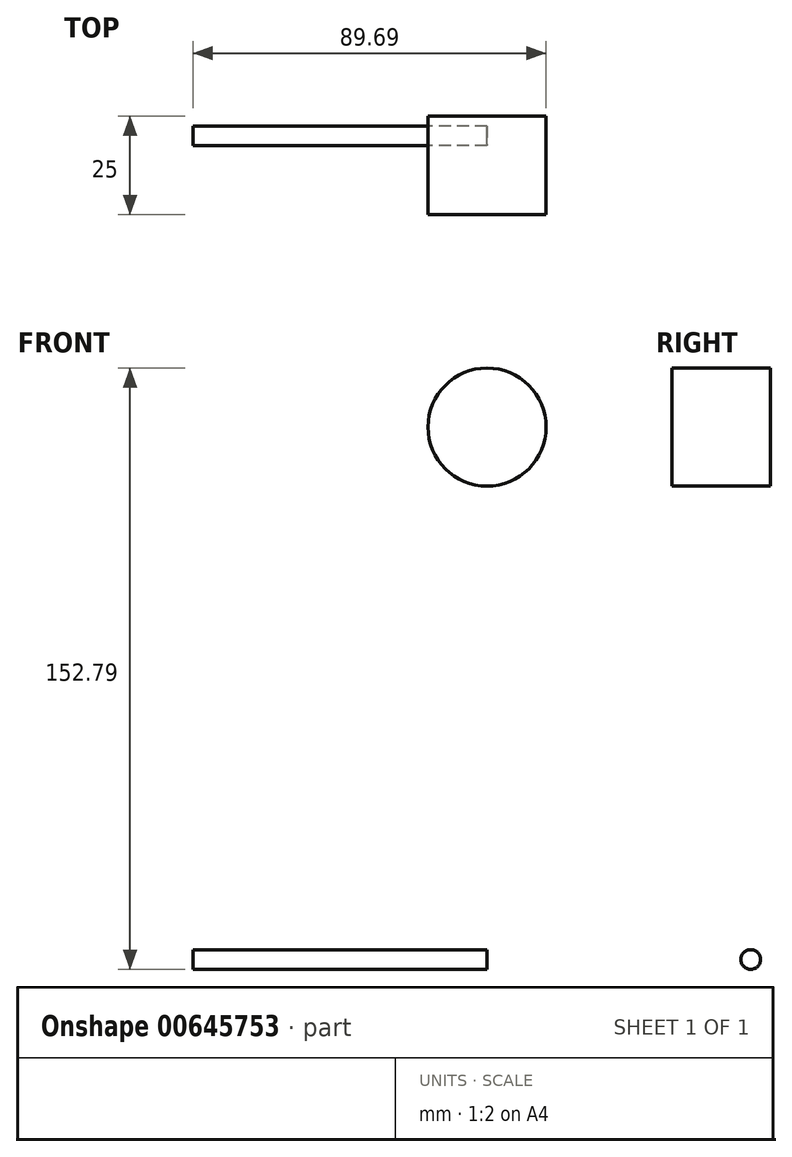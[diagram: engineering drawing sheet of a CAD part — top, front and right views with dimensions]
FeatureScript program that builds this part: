
annotation { "Feature Type Name" : "Feature", "Feature Type Description" : "" }
export const myFeature = defineFeature(function(context is Context, id is Id, definition is map)
    precondition{}
    {
        {
            var Q0;
            Q0=qCreatedBy(makeId("Front.planeOp"),FACE);
            var sketch = newSketch(context, id + "F0", { "sketchPlane" : qUnion([Q0])});
            skLineSegment(sketch, "E0", {"start": v(100, 0) * mm, "end": v(25.31, 0) * mm});
            skCircle(sketch, "E1", {"center": v(100, 135.29) * mm, "radius": 15 * mm});
            skLineSegment(sketch, "E2", {"start": v(80, 135.29) * mm, "end": v(85, 135.29) * mm});
            skLineSegment(sketch, "E3", {"start": v(12.16, 22.2) * mm, "end": v(71.23, 130.1) * mm});
            skLineSegment(sketch, "E4", {"start": v(100, 135.29) * mm, "end": v(100, -96.08) * mm, "construction": true});
            skLineSegment(sketch, "E5", {"start": v(97.07, 150) * mm, "end": v(196.34, 150) * mm, "construction": true});
            skPoint(sketch, "E6.visualSharp", {"position": v(0, 0) * mm});
            skArc(sketch, "E6.filletArc", {"start": v(12.16, 22.2) * mm, "mid": v(12.4, 7.35) * mm, "end": v(25.31, 0) * mm});
            skPoint(sketch, "E7.visualSharp", {"position": v(74.07, 135.29) * mm});
            skArc(sketch, "E7.filletArc", {"start": v(80, 135.29) * mm, "mid": v(74.9, 133.9) * mm, "end": v(71.23, 130.1) * mm});
            skSolve(sketch);
        }
        {
            var Q0;
            Q0=qCreatedBy(makeId("Right.planeOp"),FACE);
            var Q1;
            Q1=sQuery(id+"F0.wireOp",VERTEX,"E0.start");
            cPlane(context, id + "F1", {"entities" : qUnion([Q0, Q1]), "cplaneType" : CPlaneType.PLANE_POINT, "offset" : 25 * mm, "width" : 150 * mm, "height" : 150 * mm});
        }
        {
            var Q0;
            Q0=qCreatedBy(id+"F1.planeOp",FACE);
            var sketch = newSketch(context, id + "F2", { "sketchPlane" : qUnion([Q0])});
            skCircle(sketch, "E8", {"center": v(0, 0) * mm, "radius": 2.5 * mm});
            skSolve(sketch);
        }
        {
            var Q0;
            Q0=qCreatedBy(makeId("Front.planeOp"),FACE);
            var sketch = newSketch(context, id + "F3", { "sketchPlane" : qUnion([Q0])});
            skLineSegment(sketch, "E9.0", {"start": v(100, 0) * mm, "end": v(25.31, 0) * mm});
            skSolve(sketch);
        }
        {
            var Q0;
            Q0=qSketchRegion(id+"F2",true);
            var Q1;
            Q1=qConstructionFilter(qBodyType(qCreatedBy(id+"F3",EDGE),BodyType.WIRE),ConstructionObject.NO);
            sweep(context, id + "F4", {"profiles" : qUnion([Q0]), "path" : qUnion([Q1])});
        }
        {
            var Q0;
            Q0=makeQuery(id+"F4.opSweep","CAP_FACE",FACE,{"disambiguationData":[OSD([sQuery(id+"F2.wireOp",EDGE,"E8"),sQuery(id+"F3.wireOp",VERTEX,"E9.0.end")])],"isStart":false});
            var sketch = newSketch(context, id + "F5", { "sketchPlane" : qUnion([Q0])});
            skCircle(sketch, "E10.0", {"center": v(0, 0) * mm, "radius": 2.5 * mm});
            skSolve(sketch);
        }
        {
            var Q0;
            Q0=qCreatedBy(makeId("Front.planeOp"),FACE);
            var sketch = newSketch(context, id + "F6", { "sketchPlane" : qUnion([Q0])});
            skArc(sketch, "E11.0", {"start": v(12.16, 22.2) * mm, "mid": v(12.4, 7.35) * mm, "end": v(25.31, 0) * mm});
            skLineSegment(sketch, "E12.0", {"start": v(12.16, 22.2) * mm, "end": v(71.23, 130.1) * mm});
            skArc(sketch, "E13.0", {"start": v(80, 135.29) * mm, "mid": v(74.9, 133.9) * mm, "end": v(71.23, 130.1) * mm});
            skLineSegment(sketch, "E14.0", {"start": v(80, 135.29) * mm, "end": v(85, 135.29) * mm});
            skLineSegment(sketch, "E15", {"start": v(85, 135.29) * mm, "end": v(93.11, 135.29) * mm});
            skSolve(sketch);
        }
        {
            var Q0;
            Q0=qCreatedBy(makeId("Front.planeOp"),FACE);
            var sketch = newSketch(context, id + "F7", { "sketchPlane" : qUnion([Q0])});
            skCircle(sketch, "E16.0", {"center": v(100, 135.29) * mm, "radius": 15 * mm});
            skSolve(sketch);
        }
        {
            var Q0;
            Q0=qSketchRegion(id+"F7",true);
            extrude(context, id + "F8", {"entities" : qUnion([Q0]), "depth" : 20 * mm});
        }
        {
            var Q0;
            Q0=makeQuery(id+"F0.imprint","IMPRINT",FACE,{"disambiguationData":[TD([[makeQuery(id+"F0.imprint","IMPRINT",EDGE,{"derivedFrom":sQuery(id+"F0.wireOp",EDGE,"E1")}),1.0]])]});
            var sketch = newSketch(context, id + "F9", { "sketchPlane" : qUnion([Q0])});
            skCircle(sketch, "E17.0", {"center": v(100, 135.29) * mm, "radius": 15 * mm});
            skSolve(sketch);
        }
        {
            var Q0;
            Q0=qSketchRegion(id+"F9",true);
            extrude(context, id + "F10", {"entities" : qUnion([Q0]), "operationType" : NewBodyOperationType.ADD, "oppositeDirection" : true, "depth" : 5 * mm});
        }
    });
